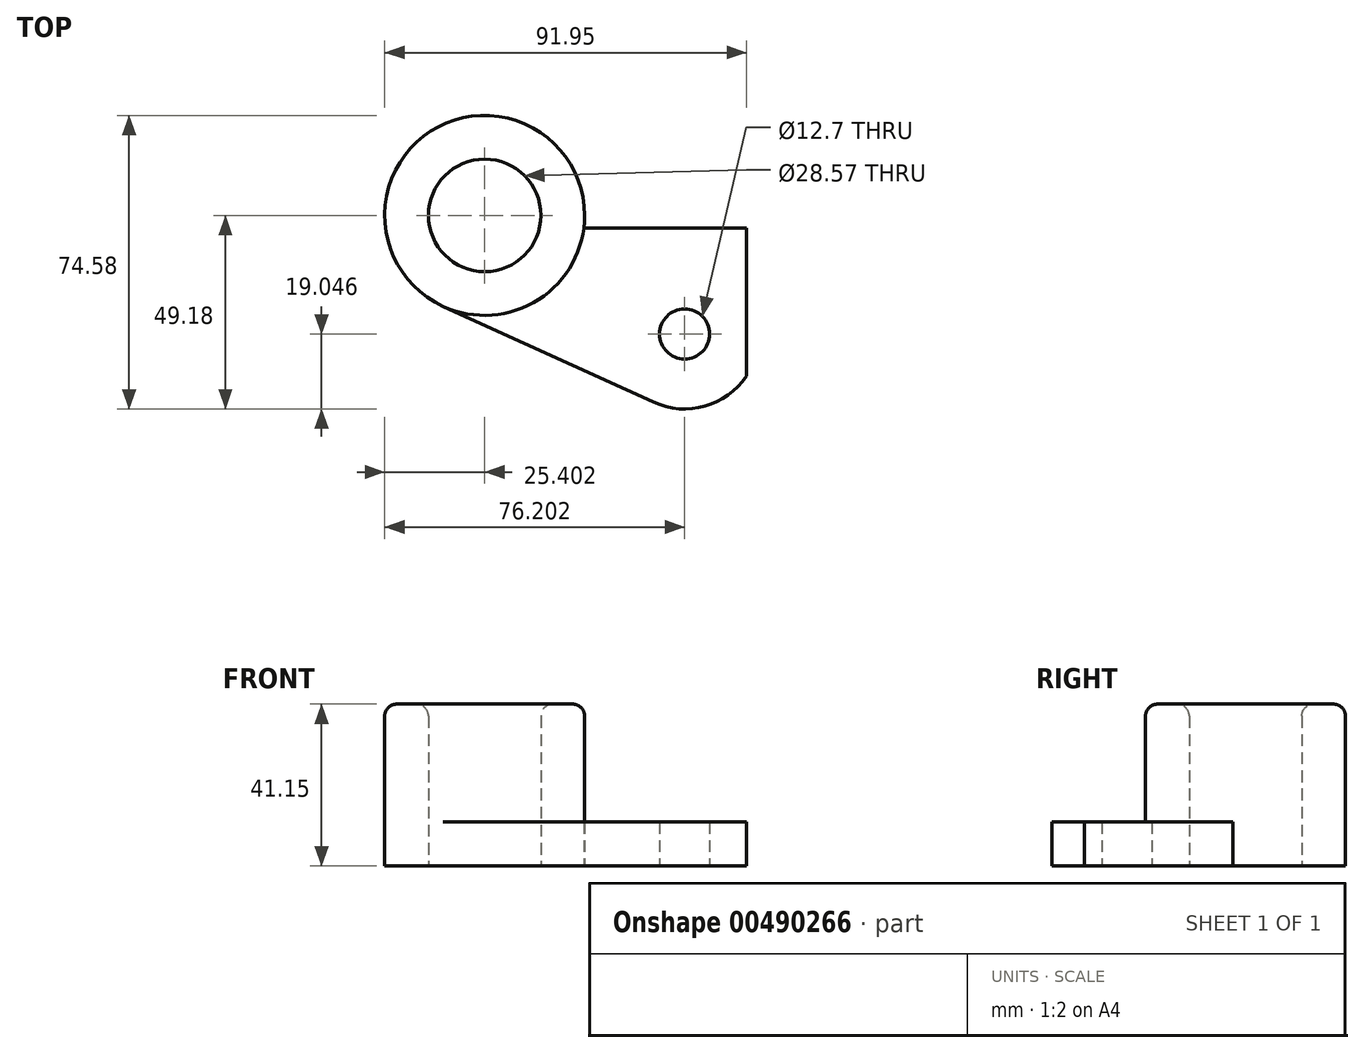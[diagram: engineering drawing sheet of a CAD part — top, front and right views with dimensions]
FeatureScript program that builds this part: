
annotation { "Feature Type Name" : "Feature", "Feature Type Description" : "" }
export const myFeature = defineFeature(function(context is Context, id is Id, definition is map)
    precondition{}
    {
        {
            var Q0;
            Q0=qCreatedBy(makeId("Top.planeOp"),FACE);
            var sketch = newSketch(context, id + "F0", { "sketchPlane" : qUnion([Q0])});
            skCircle(sketch, "E0", {"center": v(-66.55, 0) * mm, "radius": 25.4 * mm});
            skArc(sketch, "E1", {"start": v(-23.65, -47.47) * mm, "mid": v(-5.44, -46.16) * mm, "end": v(3.3, -30.13) * mm});
            skArc(sketch, "E2", {"start": v(3.3, 28.85) * mm, "mid": v(-5.28, 44.76) * mm, "end": v(-23.3, 46.34) * mm});
            skLineSegment(sketch, "E3", {"start": v(-76.61, 23.32) * mm, "end": v(-23.3, 46.34) * mm});
            skLineSegment(sketch, "E4", {"start": v(-77.08, -23.11) * mm, "end": v(-23.65, -47.47) * mm});
            skLineSegment(sketch, "E5", {"start": v(3.3, 28.85) * mm, "end": v(3.3, -30.13) * mm});
            skCircle(sketch, "E6", {"center": v(-15.75, 28.85) * mm, "radius": 6.35 * mm});
            skCircle(sketch, "E7", {"center": v(-15.75, -30.13) * mm, "radius": 6.35 * mm});
            skCircle(sketch, "E8", {"center": v(-66.55, 0) * mm, "radius": 14.29 * mm});
            skPoint(sketch, "E9", {"position": v(0, 0) * mm});
            skPoint(sketch, "E10", {"position": v(3.3, 0) * mm});
            skLineSegment(sketch, "E11", {"start": v(0, 0) * mm, "end": v(0, 3.18) * mm});
            skLineSegment(sketch, "E12", {"start": v(0, 3.18) * mm, "end": v(0, 0) * mm});
            skLineSegment(sketch, "E13", {"start": v(0, 0) * mm, "end": v(0, -3.18) * mm});
            skLineSegment(sketch, "E14", {"start": v(0, 3.18) * mm, "end": v(-41.35, 3.17) * mm});
            skLineSegment(sketch, "E15", {"start": v(0, -3.18) * mm, "end": v(-41.35, -3.18) * mm});
            skCircle(sketch, "E16", {"center": v(-66.55, 0) * mm, "radius": 16.26 * mm});
            skLineSegment(sketch, "E17", {"start": v(0, -3.18) * mm, "end": v(0, -40.85) * mm});
            skLineSegment(sketch, "E18", {"start": v(0, 3.18) * mm, "end": v(0, 39.57) * mm});
            skSolve(sketch);
        }
        {
            var Q0;
            Q0=makeQuery(id+"F0.imprint","IMPRINT",FACE,{"disambiguationData":[TD([[makeQuery(id+"F0.imprint","IMPRINT",EDGE,{"derivedFrom":sQuery(id+"F0.wireOp",EDGE,"E1")}),1.0]])]});
            var Q1;
            Q1=makeQuery(id+"F0.imprint","IMPRINT",FACE,{"disambiguationData":[TD([[makeQuery(id+"F0.imprint","IMPRINT",EDGE,{"derivedFrom":sQuery(id+"F0.wireOp",EDGE,"E12")}),-1.0]])]});
            extrude(context, id + "F1", {"entities" : qUnion([Q0, Q1]), "depth" : 11.18 * mm});
        }
        {
            var Q0;
            Q0=makeQuery(id+"F0.imprint","IMPRINT",FACE,{"disambiguationData":[TD([[makeQuery(id+"F0.imprint","IMPRINT",EDGE,{"derivedFrom":sQuery(id+"F0.wireOp",EDGE,"E8")}),-1.0]])]});
            var Q1;
            Q1=makeQuery(id+"F0.imprint","IMPRINT",FACE,{"disambiguationData":[TD([[makeQuery(id+"F0.imprint","IMPRINT",EDGE,{"derivedFrom":sQuery(id+"F0.wireOp",EDGE,"E16")}),-1.0]])]});
            extrude(context, id + "F2", {"entities" : qUnion([Q0, Q1]), "operationType" : NewBodyOperationType.ADD, "depth" : 41.15 * mm});
        }
        {
            var Q0;
            Q0=makeQuery(id+"F2.opExtrude","CAP_EDGE",EDGE,{"disambiguationData":[OSD([sQuery(id+"F0.wireOp",EDGE,"E0")])],"isStart":false});
            fillet(context, id + "F3", {"entities" : qUnion([Q0]), "radius" : 3.05 * mm, "tangentPropagation" : true, "allowEdgeOverflow" : false});
        }
        {
            var Q0;
            Q0=makeQuery(id+"F2.opExtrude","CAP_EDGE",EDGE,{"disambiguationData":[OSD([sQuery(id+"F0.wireOp",EDGE,"E8")])],"isStart":false});
            fillet(context, id + "F4", {"entities" : qUnion([Q0]), "radius" : 3.05 * mm, "tangentPropagation" : true, "allowEdgeOverflow" : false});
        }
    });
